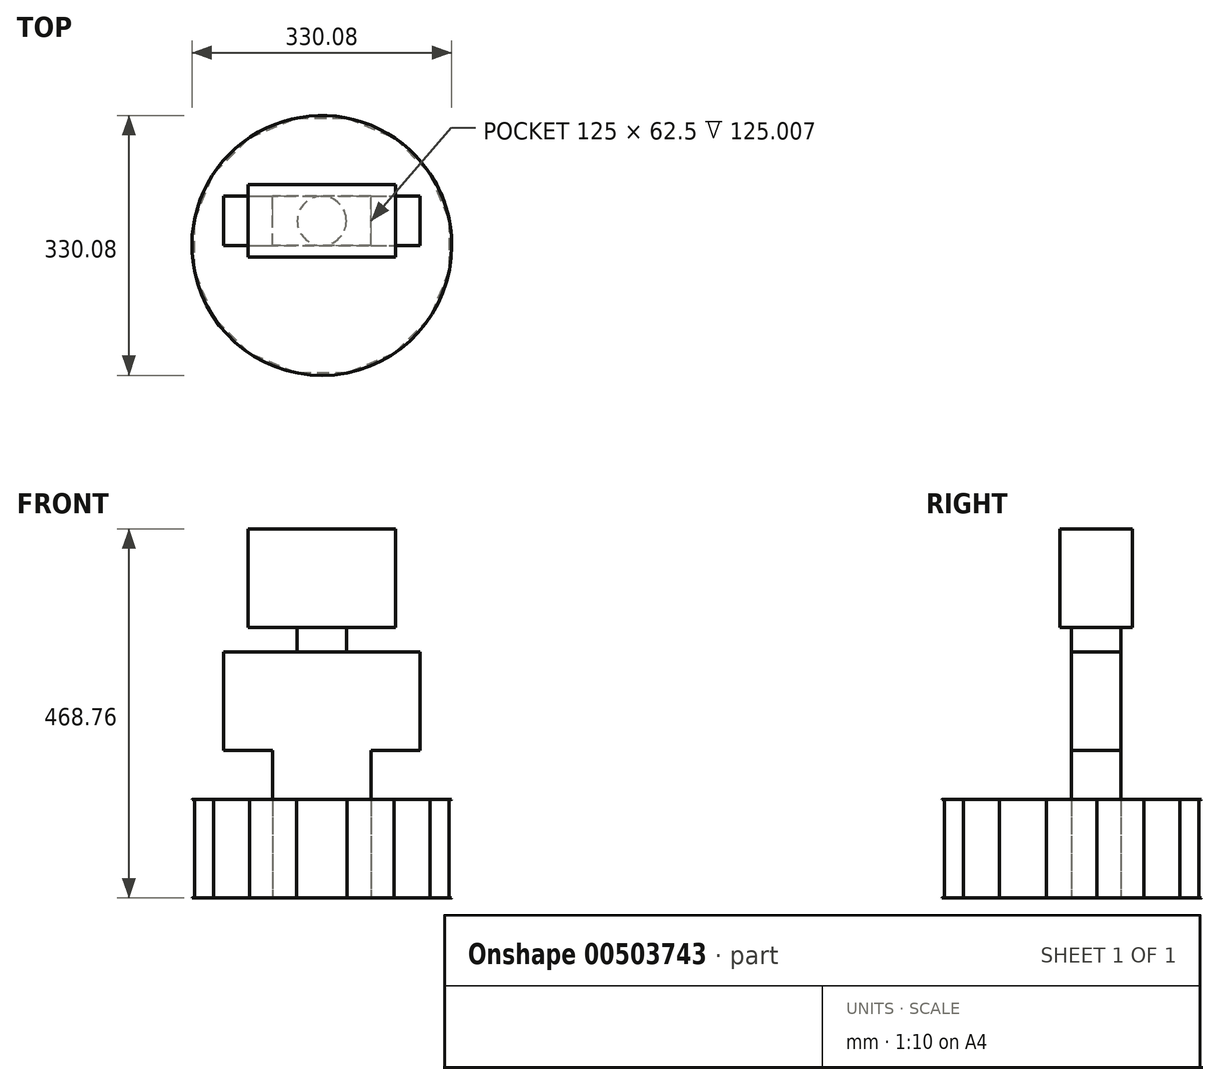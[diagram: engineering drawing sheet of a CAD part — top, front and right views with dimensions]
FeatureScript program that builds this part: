
annotation { "Feature Type Name" : "Feature", "Feature Type Description" : "" }
export const myFeature = defineFeature(function(context is Context, id is Id, definition is map)
    precondition{}
    {
        {
            assignVariable(context, id + "F0", {"name" : "Thickness", "anyValue" : 3 / 406.4 * mm});
        }
        {
            assignVariable(context, id + "F1", {"name" : "PanelHeight", "anyValue" : 125 * mm});
        }
        {
            assignVariable(context, id + "F2", {"name" : "PanelWidth", "anyValue" : getVariable(context, 'PanelHeight') / 2});
        }
        {
            var Q0;
            Q0=qCreatedBy(makeId("Top.planeOp"),FACE);
            var sketch = newSketch(context, id + "F3", { "sketchPlane" : qUnion([Q0])});
            skCircle(sketch, "E0", {"center": v(0, 0) * mm, "radius": 165.04 * mm});
            skCircle(sketch, "E1.cCircle", {"center": v(0, 0) * mm, "radius": 165.04 * mm, "construction": true});
            skLineSegment(sketch, "E1.0", {"start": v(-32.2, 161.87) * mm, "end": v(32.2, 161.87) * mm});
            skLineSegment(sketch, "E1.1", {"start": v(32.2, 161.87) * mm, "end": v(91.7, 137.22) * mm});
            skLineSegment(sketch, "E1.2", {"start": v(91.7, 137.22) * mm, "end": v(137.22, 91.7) * mm});
            skLineSegment(sketch, "E1.3", {"start": v(137.22, 91.7) * mm, "end": v(161.87, 32.2) * mm});
            skLineSegment(sketch, "E1.4", {"start": v(161.87, 32.2) * mm, "end": v(161.87, -32.2) * mm});
            skLineSegment(sketch, "E1.5", {"start": v(161.87, -32.2) * mm, "end": v(137.22, -91.7) * mm});
            skLineSegment(sketch, "E1.6", {"start": v(137.22, -91.7) * mm, "end": v(91.7, -137.22) * mm});
            skLineSegment(sketch, "E1.7", {"start": v(91.7, -137.22) * mm, "end": v(32.2, -161.87) * mm});
            skLineSegment(sketch, "E1.8", {"start": v(32.2, -161.87) * mm, "end": v(-32.2, -161.87) * mm});
            skLineSegment(sketch, "E1.9", {"start": v(-32.2, -161.87) * mm, "end": v(-91.7, -137.22) * mm});
            skLineSegment(sketch, "E1.10", {"start": v(-91.7, -137.22) * mm, "end": v(-137.22, -91.7) * mm});
            skLineSegment(sketch, "E1.11", {"start": v(-137.22, -91.7) * mm, "end": v(-161.87, -32.2) * mm});
            skLineSegment(sketch, "E1.12", {"start": v(-161.87, -32.2) * mm, "end": v(-161.87, 32.2) * mm});
            skLineSegment(sketch, "E1.13", {"start": v(-161.87, 32.2) * mm, "end": v(-137.22, 91.7) * mm});
            skLineSegment(sketch, "E1.14", {"start": v(-137.22, 91.7) * mm, "end": v(-91.7, 137.22) * mm});
            skLineSegment(sketch, "E1.15", {"start": v(-91.7, 137.22) * mm, "end": v(-32.2, 161.87) * mm});
            skLineSegment(sketch, "E2.bottom", {"start": v(-31.25, -161.87) * mm, "end": v(31.25, -161.87) * mm, "construction": true});
            skLineSegment(sketch, "E2.top", {"start": v(-31.25, -157.1) * mm, "end": v(31.25, -157.1) * mm, "construction": true});
            skLineSegment(sketch, "E2.left", {"start": v(-31.25, -161.87) * mm, "end": v(-31.25, -157.1) * mm, "construction": true});
            skLineSegment(sketch, "E2.right", {"start": v(31.25, -161.87) * mm, "end": v(31.25, -157.1) * mm, "construction": true});
            skPoint(sketch, "E3", {"position": v(0, -161.87) * mm});
            skLineSegment(sketch, "E4", {"start": v(-31.25, -157.1) * mm, "end": v(-32.2, -161.87) * mm, "construction": true});
            skLineSegment(sketch, "E5.bottom", {"start": v(62.5, 0) * mm, "end": v(-62.5, 0) * mm});
            skLineSegment(sketch, "E5.top", {"start": v(62.5, 62.5) * mm, "end": v(-62.5, 62.5) * mm});
            skLineSegment(sketch, "E5.left", {"start": v(62.5, 0) * mm, "end": v(62.5, 62.5) * mm});
            skLineSegment(sketch, "E5.right", {"start": v(-62.5, 0) * mm, "end": v(-62.5, 62.5) * mm});
            skPoint(sketch, "E5.middle", {"position": v(0, 31.25) * mm});
            skSolve(sketch);
        }
        {
            var Q0;
            Q0 = qSketchRegion(id + "F3", true);
            var Q1;
            Q1=makeQuery(id+"F3.imprint","IMPRINT",FACE,{"disambiguationData":[TD([[makeQuery(id+"F3.imprint","IMPRINT",EDGE,{"derivedFrom":sQuery(id+"F3.wireOp",EDGE,"6pC26LJY-wfZ2-4esW-fWIu-mkhxHvNKxMJP.bottom")}),-1.0]])]});
            var Q2;
            Q2=makeQuery(id+"F3.imprint","IMPRINT",FACE,{"disambiguationData":[TD([[makeQuery(id+"F3.imprint","IMPRINT",EDGE,{"derivedFrom":sQuery(id+"F3.wireOp",EDGE,"E5.bottom")}),-1.0]])]});
            extrude(context, id + "F4", {"entities" : qUnion([Q0, Q1, Q2]), "oppositeDirection" : true, "depth" : getVariable(context, 'Thickness'), "offsetDistance" : 25 * mm});
        }
        {
            var Q0;
            Q0=makeQuery(id+"F3.imprint","IMPRINT",FACE,{"disambiguationData":[TD([[makeQuery(id+"F3.imprint","IMPRINT",EDGE,{"derivedFrom":sQuery(id+"F3.wireOp",EDGE,"E1.0")}),-1.0]])]});
            var Q1;
            Q1=makeQuery(id+"F3.imprint","IMPRINT",FACE,{"disambiguationData":[TD([[makeQuery(id+"F3.imprint","IMPRINT",EDGE,{"derivedFrom":sQuery(id+"F3.wireOp",EDGE,"E5.bottom")}),-1.0]])]});
            extrude(context, id + "F5", {"entities" : qUnion([Q0, Q1]), "operationType" : NewBodyOperationType.ADD, "depth" : getVariable(context, 'PanelHeight'), "offsetDistance" : 25 * mm});
        }
        {
            var Q0;
            Q0=makeQuery(id+"F5.opExtrude","CAP_FACE",FACE,{"disambiguationData":[OSD([sQuery(id+"F3.wireOp",EDGE,"E1.0"),sQuery(id+"F3.wireOp",EDGE,"E1.1"),sQuery(id+"F3.wireOp",EDGE,"E1.2"),sQuery(id+"F3.wireOp",EDGE,"E1.3"),sQuery(id+"F3.wireOp",EDGE,"E1.4"),sQuery(id+"F3.wireOp",EDGE,"E1.5"),sQuery(id+"F3.wireOp",EDGE,"E1.6"),sQuery(id+"F3.wireOp",EDGE,"E1.7"),sQuery(id+"F3.wireOp",EDGE,"E1.8"),sQuery(id+"F3.wireOp",EDGE,"E1.9"),sQuery(id+"F3.wireOp",EDGE,"E1.10"),sQuery(id+"F3.wireOp",EDGE,"E1.11"),sQuery(id+"F3.wireOp",EDGE,"E1.12"),sQuery(id+"F3.wireOp",EDGE,"E1.13"),sQuery(id+"F3.wireOp",EDGE,"E1.14"),sQuery(id+"F3.wireOp",EDGE,"E1.15")])],"isStart":false});
            var sketch = newSketch(context, id + "F6", { "sketchPlane" : qUnion([Q0])});
            skCircle(sketch, "E6.0", {"center": v(0, 0) * mm, "radius": 165.04 * mm});
            skSolve(sketch);
        }
        {
            var Q0;
            Q0 = qSketchRegion(id + "F6", true);
            extrude(context, id + "F7", {"entities" : qUnion([Q0]), "operationType" : NewBodyOperationType.ADD, "depth" : getVariable(context, 'Thickness'), "offsetDistance" : 25 * mm});
        }
        {
            var Q0;
            Q0=makeQuery(id+"F3.imprint","IMPRINT",FACE,{"disambiguationData":[TD([[makeQuery(id+"F3.imprint","IMPRINT",EDGE,{"derivedFrom":sQuery(id+"F3.wireOp",EDGE,"E5.bottom")}),-1.0]])]});
            extrude(context, id + "F8", {"entities" : qUnion([Q0]), "depth" : 386 * mm, "offsetDistance" : 25 * mm});
        }
        {
            var Q0;
            Q0=makeQuery(id+"F8.opExtrude","SWEPT_BODY",BODY,{"disambiguationData":[OSD([sQuery(id+"F3.wireOp",EDGE,"E5.bottom"),sQuery(id+"F3.wireOp",EDGE,"E5.top"),sQuery(id+"F3.wireOp",EDGE,"E5.left"),sQuery(id+"F3.wireOp",EDGE,"E5.right")])]});
            var Q1;
            Q1=makeQuery(id+"F4.opExtrude","SWEPT_BODY",BODY,{"disambiguationData":[OSD([sQuery(id+"F3.wireOp",EDGE,"E0")])]});
            booleanBodies(context, id + "F9", {"operationType" : BooleanOperationType.SUBTRACTION, "tools" : qUnion([Q0]), "targets" : qUnion([Q1])});
        }
        {
            var Q0;
            Q0=makeQuery(id+"F9.opBoolean","COPY",FACE,{"derivedFrom":makeQuery(id+"F8.opExtrude","SWEPT_FACE",FACE,{"disambiguationData":[OSD([sQuery(id+"F3.wireOp",EDGE,"E5.top")])]})});
            var sketch = newSketch(context, id + "F10", { "sketchPlane" : qUnion([Q0])});
            skLineSegment(sketch, "E7.bottom", {"start": v(-62.5, 0) * mm, "end": v(62.5, 0) * mm});
            skLineSegment(sketch, "E7.left", {"start": v(-62.5, 0) * mm, "end": v(-62.5, 187.5) * mm});
            skLineSegment(sketch, "E7.right", {"start": v(62.5, 0) * mm, "end": v(62.5, 187.5) * mm});
            skPoint(sketch, "E7.middle", {"position": v(0, 125) * mm});
            skLineSegment(sketch, "E8.top", {"start": v(-125, 187.5) * mm, "end": v(-62.5, 187.5) * mm});
            skLineSegment(sketch, "E8.left", {"start": v(-125, 187.5) * mm, "end": v(-125, 312.5) * mm});
            skLineSegment(sketch, "E8.right", {"start": v(125, 187.5) * mm, "end": v(125, 312.5) * mm});
            skPoint(sketch, "E8.middle", {"position": v(0, 250) * mm});
            skLineSegment(sketch, "E9", {"start": v(0, 250) * mm, "end": v(0, 125) * mm, "construction": true});
            skLineSegment(sketch, "E10.trimOffspring", {"start": v(62.5, 187.5) * mm, "end": v(125, 187.5) * mm});
            skLineSegment(sketch, "E11", {"start": v(-125, 312.5) * mm, "end": v(125, 312.5) * mm});
            skSolve(sketch);
        }
        {
            var Q0;
            Q0 = qSketchRegion(id + "F10", true);
            extrude(context, id + "F11", {"entities" : qUnion([Q0]), "depth" : getVariable(context, 'PanelWidth'), "offsetDistance" : 25 * mm});
        }
        {
            var Q0;
            Q0=makeQuery(id+"F11.opExtrude","SWEPT_FACE",FACE,{"disambiguationData":[OSD([sQuery(id+"F10.wireOp",EDGE,"E11")])]});
            var sketch = newSketch(context, id + "F12", { "sketchPlane" : qUnion([Q0])});
            skCircle(sketch, "E12", {"center": v(0, 31.25) * mm, "radius": 31.25 * mm});
            skSolve(sketch);
        }
        {
            var Q0;
            {var subQ0=sQuery(id+"F12.wireOp",EDGE,"E12");var subQ1=sQuery(id+"F10.wireOp",EDGE,"E11");var subQ2=makeQuery(id+"F12.imprint","INTERSECT",VERTEX,{"derivedFrom":[makeQuery(id+"F11.opExtrude","CAP_EDGE",EDGE,{"disambiguationData":[OSD([subQ1])],"isStart":true}),subQ0]});Q0=makeQuery(id+"F12.imprint","IMPRINT",FACE,{"disambiguationData":[TD([[makeQuery(id+"F12.imprint","IMPRINT",EDGE,{"disambiguationData":[TD([[subQ2,-1.0]])],"derivedFrom":subQ0}),1.0]])]});}
            extrude(context, id + "F13", {"entities" : qUnion([Q0]), "depth" : getVariable(context, 'PanelWidth') / 2, "offsetDistance" : 25 * mm});
        }
        {
            var Q0;
            Q0=makeQuery(id+"F13.opExtrude","CAP_FACE",FACE,{"disambiguationData":[OSD([sQuery(id+"F12.wireOp",EDGE,"E12")])],"isStart":false});
            var sketch = newSketch(context, id + "F14", { "sketchPlane" : qUnion([Q0])});
            skLineSegment(sketch, "E13.bottom", {"start": v(93.75, -14.87) * mm, "end": v(-93.75, -14.88) * mm});
            skLineSegment(sketch, "E13.top", {"start": v(93.75, 77.38) * mm, "end": v(-93.75, 77.38) * mm});
            skLineSegment(sketch, "E13.left", {"start": v(93.75, -14.87) * mm, "end": v(93.75, 77.38) * mm});
            skLineSegment(sketch, "E13.right", {"start": v(-93.75, -14.88) * mm, "end": v(-93.75, 77.38) * mm});
            skPoint(sketch, "E13.middle", {"position": v(0, 31.25) * mm});
            skSolve(sketch);
        }
        {
            var Q0;
            Q0 = qSketchRegion(id + "F14", true);
            extrude(context, id + "F15", {"entities" : qUnion([Q0]), "depth" : getVariable(context, 'PanelHeight'), "offsetDistance" : 25 * mm});
        }
    });
